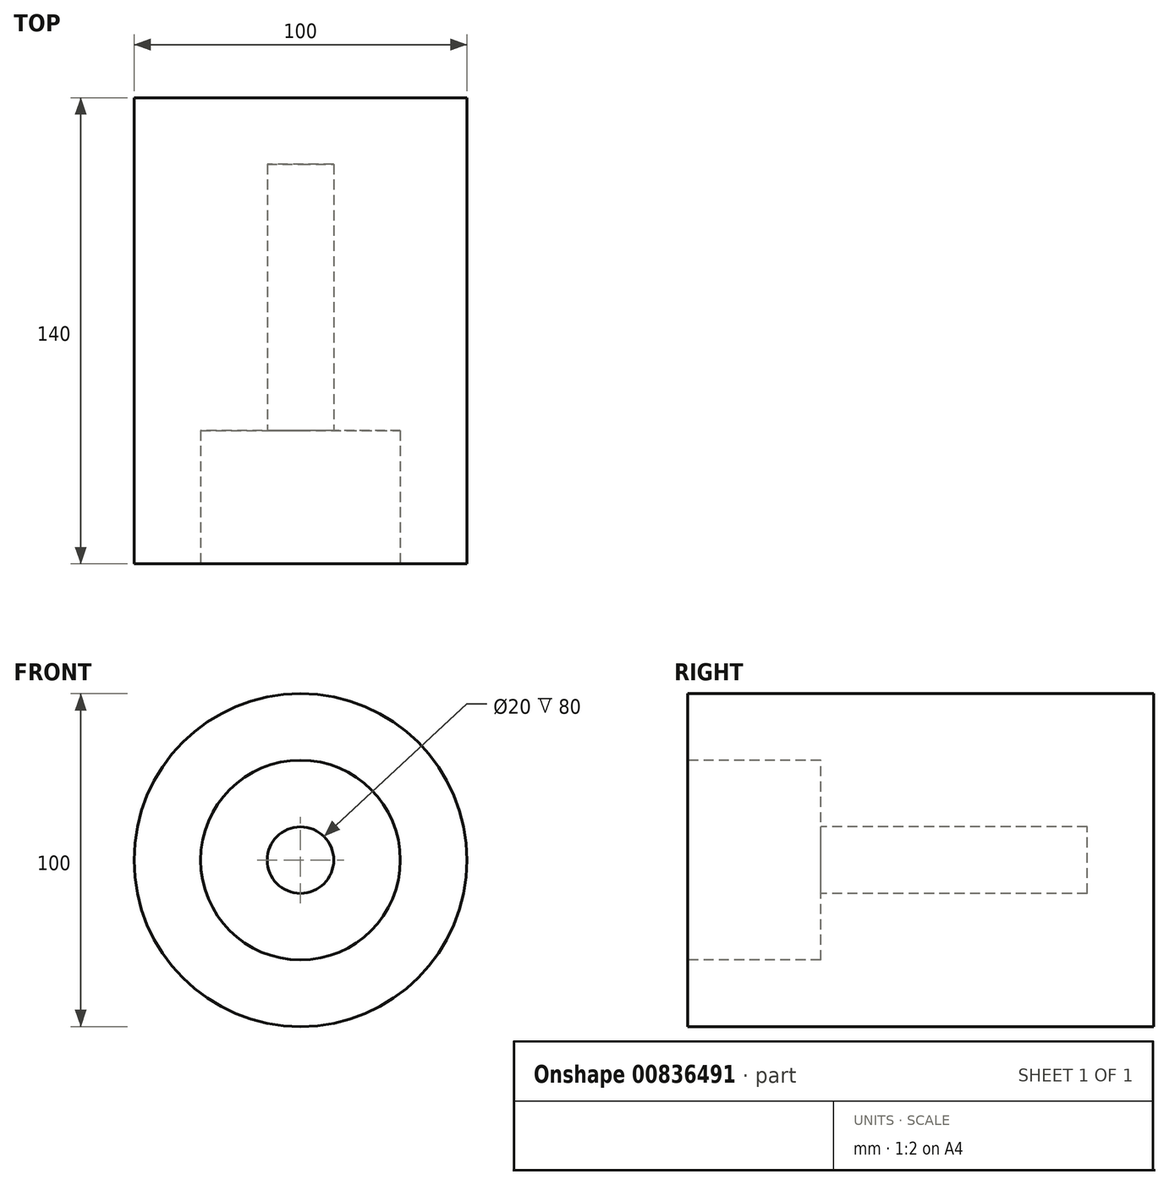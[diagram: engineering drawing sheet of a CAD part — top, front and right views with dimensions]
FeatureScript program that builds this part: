
annotation { "Feature Type Name" : "Feature", "Feature Type Description" : "" }
export const myFeature = defineFeature(function(context is Context, id is Id, definition is map)
    precondition{}
    {
        {
            var Q0;
            Q0=qCreatedBy(makeId("Front.planeOp"),FACE);
            var sketch = newSketch(context, id + "F0", { "sketchPlane" : qUnion([Q0])});
            skCircle(sketch, "E0", {"center": v(0, 0) * mm, "radius": 50 * mm});
            skSolve(sketch);
        }
        {
            var Q0;
            Q0 = qSketchRegion(id + "F0", true);
            extrude(context, id + "F1", {"entities" : qUnion([Q0]), "depth" : 140 * mm, "offsetDistance" : 25 * mm});
        }
        {
            var Q0;
            Q0=makeQuery(id+"F1.opExtrude","CAP_FACE",FACE,{"disambiguationData":[OSD([sQuery(id+"F0.wireOp",EDGE,"E0")])],"isStart":false});
            var sketch = newSketch(context, id + "F2", { "sketchPlane" : qUnion([Q0])});
            skCircle(sketch, "E1", {"center": v(0, 0) * mm, "radius": 10 * mm});
            skSolve(sketch);
        }
        {
            var Q0;
            Q0 = qSketchRegion(id + "F2", true);
            extrude(context, id + "F3", {"entities" : qUnion([Q0]), "operationType" : NewBodyOperationType.REMOVE, "oppositeDirection" : true, "depth" : 120 * mm, "offsetDistance" : 25 * mm});
        }
        {
            var Q0;
            Q0=makeQuery(id+"F1.opExtrude","CAP_FACE",FACE,{"disambiguationData":[OSD([sQuery(id+"F0.wireOp",EDGE,"E0")])],"isStart":false});
            var sketch = newSketch(context, id + "F4", { "sketchPlane" : qUnion([Q0])});
            skCircle(sketch, "E2", {"center": v(0, 0) * mm, "radius": 30 * mm});
            skSolve(sketch);
        }
        {
            var Q0;
            Q0 = qSketchRegion(id + "F4", true);
            extrude(context, id + "F5", {"entities" : qUnion([Q0]), "operationType" : NewBodyOperationType.REMOVE, "oppositeDirection" : true, "depth" : 40 * mm, "offsetDistance" : 25 * mm});
        }
    });
